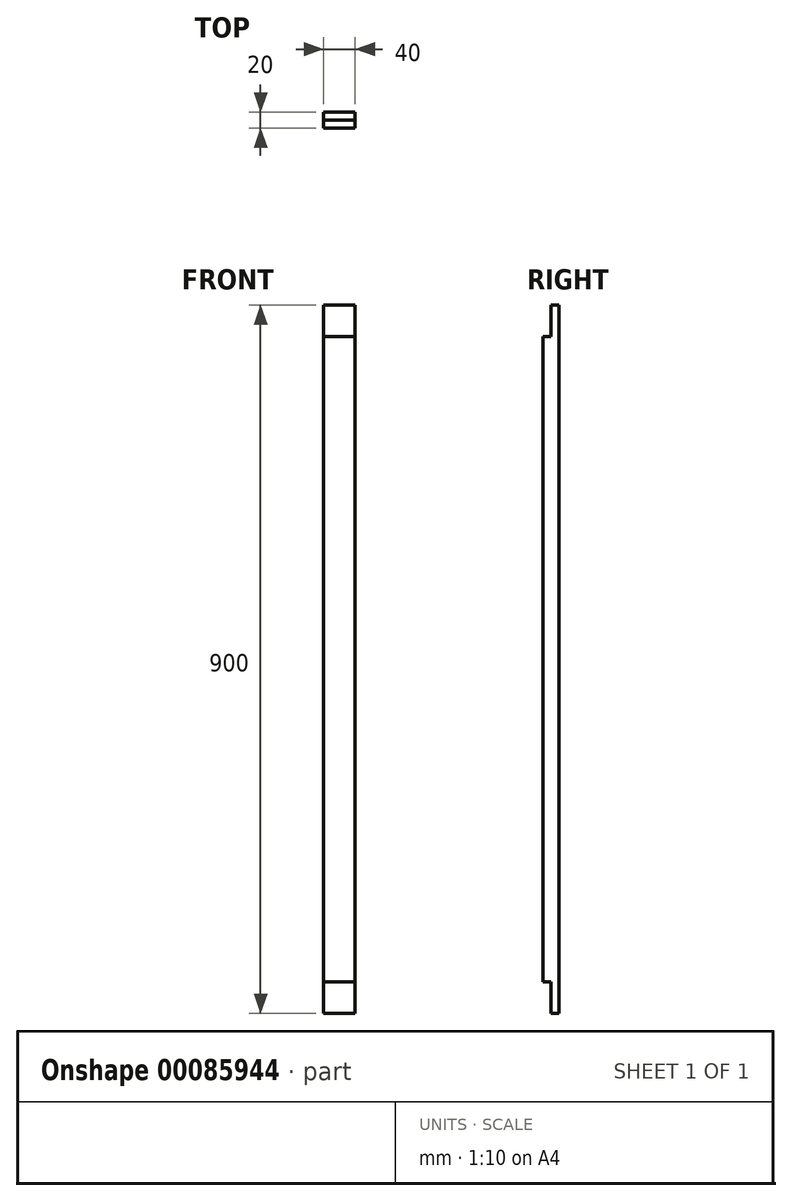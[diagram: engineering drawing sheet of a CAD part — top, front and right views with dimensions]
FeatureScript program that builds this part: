
annotation { "Feature Type Name" : "Feature", "Feature Type Description" : "" }
export const myFeature = defineFeature(function(context is Context, id is Id, definition is map)
    precondition{}
    {
        {
            var Q0;
            Q0=makeQuery(id+"FG9kwGrBFYMyLTM_0.opExtrude","CAP_FACE",FACE,{"disambiguationData":[OSD([sQuery(id+"Fa9PPX21gxXJaQZ_0.wireOp",EDGE,"gOYDLFoV-yjyc-MAcR-eyRR-AS494CBYp5cq"),sQuery(id+"Fa9PPX21gxXJaQZ_0.wireOp",EDGE,"lm9vaZYr-2K7i-kmaF-rlea-WMQxN018Bubt"),sQuery(id+"Fa9PPX21gxXJaQZ_0.wireOp",EDGE,"3NtCanxF-rbRE-YtSa-ATdM-2x4zHrKcNhKx"),sQuery(id+"Fa9PPX21gxXJaQZ_0.wireOp",EDGE,"aYrkMxfi-21Mw-EvYH-VemH-VzoiSDv8W9wj"),sQuery(id+"Fa9PPX21gxXJaQZ_0.wireOp",EDGE,"PEP8k3KO-CcRg-1Apg-lGj5-ivniBFzsYTXf"),sQuery(id+"Fa9PPX21gxXJaQZ_0.wireOp",EDGE,"pKww28Sn-9eQe-Rgkb-dqUD-SCZ7gcrLek11"),sQuery(id+"Fa9PPX21gxXJaQZ_0.wireOp",EDGE,"UPuwfs1R-Zhn5-X8M4-OYRY-o4vc3LRBeDjN"),sQuery(id+"Fa9PPX21gxXJaQZ_0.wireOp",EDGE,"a1Nc1zX7-udch-pN3B-jKvL-MMfgIOru0FyU"),sQuery(id+"Fa9PPX21gxXJaQZ_0.wireOp",EDGE,"NO93iRp1-pqGa-UnV6-1Ato-wFwaLVSlGjmf"),sQuery(id+"Fa9PPX21gxXJaQZ_0.wireOp",EDGE,"rS70e5TO-R8LT-DVZq-JrlB-bef2KivJNTmL")])],"isStart":false});
            var sketch = newSketch(context, id + "F0", { "sketchPlane" : qUnion([Q0])});
            skLineSegment(sketch, "E0.bottom", {"start": v(-56.77, 444.99) * mm, "end": v(-31.77, 444.99) * mm});
            skLineSegment(sketch, "E0.top", {"start": v(-56.77, 374.99) * mm, "end": v(-31.77, 374.99) * mm});
            skLineSegment(sketch, "E0.left", {"start": v(-56.77, 444.99) * mm, "end": v(-56.77, 374.99) * mm});
            skLineSegment(sketch, "E0.right", {"start": v(-31.77, 444.99) * mm, "end": v(-31.77, 374.99) * mm});
            skSolve(sketch);
        }
        {
            var Q0;
            Q0=makeQuery(id+"FG9kwGrBFYMyLTM_0.opExtrude","CAP_FACE",FACE,{"disambiguationData":[OSD([sQuery(id+"Fa9PPX21gxXJaQZ_0.wireOp",EDGE,"gOYDLFoV-yjyc-MAcR-eyRR-AS494CBYp5cq"),sQuery(id+"Fa9PPX21gxXJaQZ_0.wireOp",EDGE,"lm9vaZYr-2K7i-kmaF-rlea-WMQxN018Bubt"),sQuery(id+"Fa9PPX21gxXJaQZ_0.wireOp",EDGE,"3NtCanxF-rbRE-YtSa-ATdM-2x4zHrKcNhKx"),sQuery(id+"Fa9PPX21gxXJaQZ_0.wireOp",EDGE,"aYrkMxfi-21Mw-EvYH-VemH-VzoiSDv8W9wj"),sQuery(id+"Fa9PPX21gxXJaQZ_0.wireOp",EDGE,"PEP8k3KO-CcRg-1Apg-lGj5-ivniBFzsYTXf"),sQuery(id+"Fa9PPX21gxXJaQZ_0.wireOp",EDGE,"pKww28Sn-9eQe-Rgkb-dqUD-SCZ7gcrLek11"),sQuery(id+"Fa9PPX21gxXJaQZ_0.wireOp",EDGE,"UPuwfs1R-Zhn5-X8M4-OYRY-o4vc3LRBeDjN"),sQuery(id+"Fa9PPX21gxXJaQZ_0.wireOp",EDGE,"a1Nc1zX7-udch-pN3B-jKvL-MMfgIOru0FyU"),sQuery(id+"Fa9PPX21gxXJaQZ_0.wireOp",EDGE,"NO93iRp1-pqGa-UnV6-1Ato-wFwaLVSlGjmf"),sQuery(id+"Fa9PPX21gxXJaQZ_0.wireOp",EDGE,"rS70e5TO-R8LT-DVZq-JrlB-bef2KivJNTmL")])],"isStart":false});
            var sketch = newSketch(context, id + "F1", { "sketchPlane" : qUnion([Q0])});
            skCircle(sketch, "E1", {"center": v(-21.77, 74.99) * mm, "radius": 8 * mm});
            skPoint(sketch, "E1.centerSnap0", {"position": v(-21.77, 444.99) * mm});
            skSolve(sketch);
        }
        {
            var Q0;
            Q0=qCreatedBy(makeId("Front.planeOp"),FACE);
            var sketch = newSketch(context, id + "F2", { "sketchPlane" : qUnion([Q0])});
            skLineSegment(sketch, "E2.bottom", {"start": v(20, 450) * mm, "end": v(-20, 450) * mm});
            skLineSegment(sketch, "E2.top", {"start": v(20, -450) * mm, "end": v(-20, -450) * mm});
            skLineSegment(sketch, "E2.left", {"start": v(20, 450) * mm, "end": v(20, -450) * mm});
            skLineSegment(sketch, "E2.right", {"start": v(-20, 450) * mm, "end": v(-20, -450) * mm});
            skPoint(sketch, "E2.middle", {"position": v(0, 0) * mm});
            skSolve(sketch);
        }
        {
            var Q0;
            Q0=makeQuery(id+"F2.imprint","IMPRINT",FACE,{"disambiguationData":[TD([[makeQuery(id+"F2.imprint","IMPRINT",EDGE,{"derivedFrom":sQuery(id+"F2.wireOp",EDGE,"E2.bottom")}),1.0]])]});
            extrude(context, id + "F3", {"entities" : qUnion([Q0]), "depth" : 20 * mm});
        }
        {
            var Q0;
            Q0=makeQuery(id+"F3.opExtrude","CAP_FACE",FACE,{"disambiguationData":[OSD([sQuery(id+"F2.wireOp",EDGE,"E2.bottom"),sQuery(id+"F2.wireOp",EDGE,"E2.top"),sQuery(id+"F2.wireOp",EDGE,"E2.left"),sQuery(id+"F2.wireOp",EDGE,"E2.right")])],"isStart":false});
            var sketch = newSketch(context, id + "F4", { "sketchPlane" : qUnion([Q0])});
            skLineSegment(sketch, "E3.bottom", {"start": v(-20, 450) * mm, "end": v(20, 450) * mm});
            skLineSegment(sketch, "E3.top", {"start": v(-20, 410) * mm, "end": v(20, 410) * mm});
            skLineSegment(sketch, "E3.left", {"start": v(-20, 450) * mm, "end": v(-20, 410) * mm});
            skLineSegment(sketch, "E3.right", {"start": v(20, 450) * mm, "end": v(20, 410) * mm});
            skSolve(sketch);
        }
        {
            var Q0;
            Q0=makeQuery(id+"F4.imprint","IMPRINT",FACE,{"disambiguationData":[TD([[makeQuery(id+"F4.imprint","IMPRINT",EDGE,{"derivedFrom":sQuery(id+"F4.wireOp",EDGE,"E3.bottom")}),1.0]])]});
            extrude(context, id + "F5", {"entities" : qUnion([Q0]), "operationType" : NewBodyOperationType.REMOVE, "oppositeDirection" : true, "depth" : 10 * mm});
        }
        {
            var Q0;
            Q0=makeQuery(id+"F3.opExtrude","CAP_FACE",FACE,{"disambiguationData":[OSD([sQuery(id+"F2.wireOp",EDGE,"E2.bottom"),sQuery(id+"F2.wireOp",EDGE,"E2.top"),sQuery(id+"F2.wireOp",EDGE,"E2.left"),sQuery(id+"F2.wireOp",EDGE,"E2.right")])],"isStart":false});
            var sketch = newSketch(context, id + "F6", { "sketchPlane" : qUnion([Q0])});
            skLineSegment(sketch, "E4.bottom", {"start": v(20, -450) * mm, "end": v(-20, -450) * mm});
            skLineSegment(sketch, "E4.top", {"start": v(20, -410) * mm, "end": v(-20, -410) * mm});
            skLineSegment(sketch, "E4.left", {"start": v(20, -450) * mm, "end": v(20, -410) * mm});
            skLineSegment(sketch, "E4.right", {"start": v(-20, -450) * mm, "end": v(-20, -410) * mm});
            skSolve(sketch);
        }
        {
            var Q0;
            Q0=makeQuery(id+"F6.imprint","IMPRINT",FACE,{"disambiguationData":[TD([[makeQuery(id+"F6.imprint","IMPRINT",EDGE,{"derivedFrom":sQuery(id+"F6.wireOp",EDGE,"E4.bottom")}),-1.0]])]});
            extrude(context, id + "F7", {"entities" : qUnion([Q0]), "operationType" : NewBodyOperationType.REMOVE, "oppositeDirection" : true, "depth" : 10 * mm});
        }
    });
